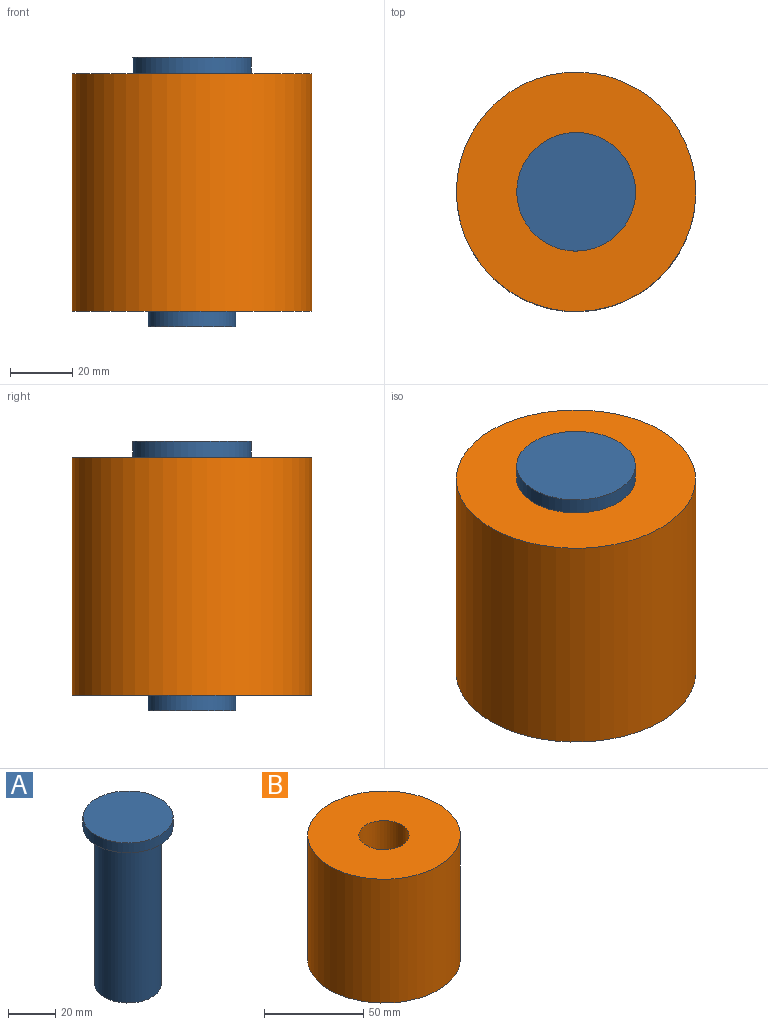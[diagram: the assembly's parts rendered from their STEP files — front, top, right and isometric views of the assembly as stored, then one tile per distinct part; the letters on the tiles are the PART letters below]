
ASSEMBLY  parts=2 mates=1
PART A: 7 faces, bbox 38.1x38.1x86.4 mm
  f0: cylinder r=14.07mm len=81.28mm, axis (0,0,-1), area 7183.6mm2, adj f1,f3
  f1: plane 28.13x28.13mm, normal (0,0,-1), area 434.5mm2, adj f0,f2
  f2: cylinder r=7.72mm len=81.28mm, axis (0,0,-1), area 3940.7mm2, adj f1,f6
  f3: plane 38.1x38.1mm, normal (0,0,-1), area 518.5mm2, adj f0,f5
  f4: plane 38.1x38.1mm, normal (0,0,1), area 1140.1mm2, adj f5
  f5: cylinder r=19.05mm len=38.1mm, axis (0,0,-1), area 608mm2, adj f3,f4
  f6: plane 15.43x15.43mm, normal (0,0,-1), area 187.1mm2, adj f2
PART B: 4 faces, bbox 76.9x76.9x76.2 mm
  f0: plane 76.86x76.86mm, normal (0,0,1), area 4138.7mm2, adj f1,f3
  f1: cylinder r=38.43mm len=76.86mm, axis (0,0,-1), area 18398.8mm2, adj f0,f2
  f2: plane 76.86x76.86mm, normal (0,0,-1), area 4138.7mm2, adj f1,f3
  f3: cylinder r=12.62mm len=76.2mm, axis (0,0,-1), area 6044mm2, adj f0,f2
PLACE A t=(4.31,-22.29,-0.79)mm
PLACE B t=(4.31,-22.29,0)mm
MATE slider A.f0 <-> B.f1  axis (0,0,-1) through (4.31,-22.29,6.3)mm
